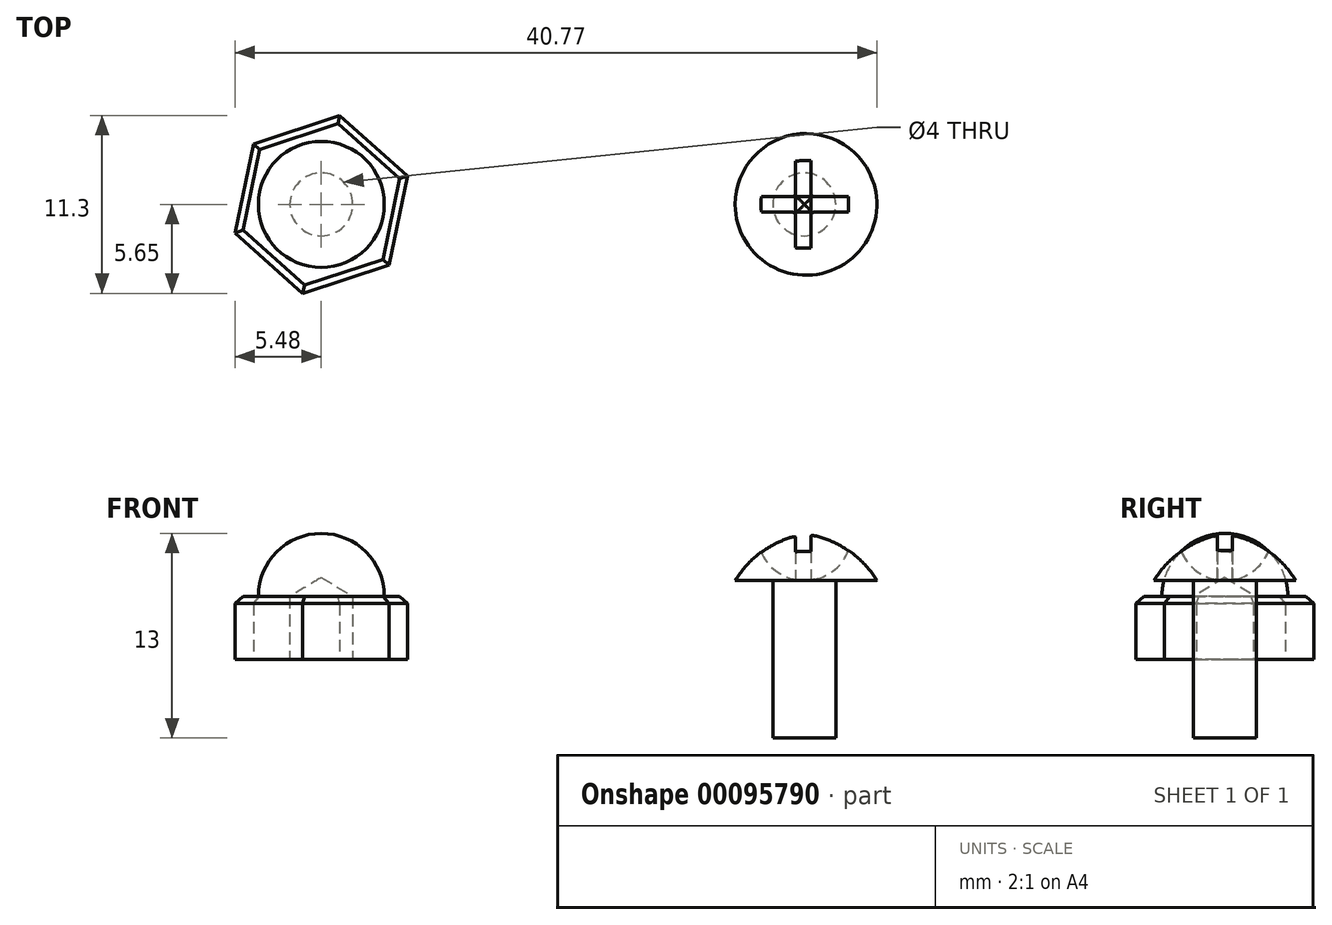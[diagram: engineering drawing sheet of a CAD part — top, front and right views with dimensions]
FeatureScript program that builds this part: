
annotation { "Feature Type Name" : "Feature", "Feature Type Description" : "" }
export const myFeature = defineFeature(function(context is Context, id is Id, definition is map)
    precondition{}
    {
        {
            var Q0;
            Q0=qCreatedBy(makeId("Top.planeOp"),FACE);
            var sketch = newSketch(context, id + "F0", { "sketchPlane" : qUnion([Q0])});
            skCircle(sketch, "E0.cCircle", {"center": v(0, 0) * mm, "radius": 5 * mm, "construction": true});
            skLineSegment(sketch, "E0.0", {"start": v(-4.3, 3.84) * mm, "end": v(1.17, 5.65) * mm});
            skLineSegment(sketch, "E0.1", {"start": v(1.17, 5.65) * mm, "end": v(5.48, 1.8) * mm});
            skLineSegment(sketch, "E0.2", {"start": v(5.48, 1.8) * mm, "end": v(4.3, -3.84) * mm});
            skLineSegment(sketch, "E0.3", {"start": v(4.3, -3.84) * mm, "end": v(-1.17, -5.65) * mm});
            skLineSegment(sketch, "E0.4", {"start": v(-1.17, -5.65) * mm, "end": v(-5.48, -1.8) * mm});
            skLineSegment(sketch, "E0.5", {"start": v(-5.48, -1.8) * mm, "end": v(-4.3, 3.84) * mm});
            skPoint(sketch, "E0.0.midPoint", {"position": v(-1.57, 4.75) * mm});
            skSolve(sketch);
        }
        {
            var Q0;
            Q0 = qSketchRegion(id + "F0", true);
            extrude(context, id + "F1", {"entities" : qUnion([Q0]), "depth" : 4 * mm});
        }
        {
            var Q0;
            Q0=makeQuery(id+"F1.opExtrude","CAP_FACE",FACE,{"disambiguationData":[OSD([sQuery(id+"F0.wireOp",EDGE,"E0.0"),sQuery(id+"F0.wireOp",EDGE,"E0.1"),sQuery(id+"F0.wireOp",EDGE,"E0.2"),sQuery(id+"F0.wireOp",EDGE,"E0.3"),sQuery(id+"F0.wireOp",EDGE,"E0.4"),sQuery(id+"F0.wireOp",EDGE,"E0.5")])],"isStart":false});
            var sketch = newSketch(context, id + "F2", { "sketchPlane" : qUnion([Q0])});
            skArc(sketch, "E1", {"start": v(-4, 0) * mm, "mid": v(0, 4) * mm, "end": v(4, 0) * mm});
            skLineSegment(sketch, "E2", {"start": v(-4, 0) * mm, "end": v(4, 0) * mm});
            skSolve(sketch);
        }
        {
            var Q0;
            Q0 = qSketchRegion(id + "F2", true);
            var Q1;
            Q1=sQuery(id+"F2.wireOp",EDGE,"E2");
            revolve(context, id + "F3", {"operationType" : NewBodyOperationType.ADD, "entities" : qUnion([Q0]), "axis" : qUnion([Q1]), "revolveType" : RevolveType.ONE_DIRECTION, "angle" : 180 * degree});
        }
        {
            var Q0;
            Q0=makeQuery(id+"F1.opExtrude","CAP_EDGE",EDGE,{"disambiguationData":[OSD([sQuery(id+"F0.wireOp",EDGE,"E0.5")])],"isStart":false});
            var Q1;
            Q1=makeQuery(id+"F1.opExtrude","CAP_EDGE",EDGE,{"disambiguationData":[OSD([sQuery(id+"F0.wireOp",EDGE,"E0.4")])],"isStart":false});
            var Q2;
            Q2=makeQuery(id+"F1.opExtrude","CAP_EDGE",EDGE,{"disambiguationData":[OSD([sQuery(id+"F0.wireOp",EDGE,"E0.3")])],"isStart":false});
            var Q3;
            Q3=makeQuery(id+"F1.opExtrude","CAP_EDGE",EDGE,{"disambiguationData":[OSD([sQuery(id+"F0.wireOp",EDGE,"E0.2")])],"isStart":false});
            var Q4;
            Q4=makeQuery(id+"F1.opExtrude","CAP_EDGE",EDGE,{"disambiguationData":[OSD([sQuery(id+"F0.wireOp",EDGE,"E0.1")])],"isStart":false});
            var Q5;
            Q5=makeQuery(id+"F1.opExtrude","CAP_EDGE",EDGE,{"disambiguationData":[OSD([sQuery(id+"F0.wireOp",EDGE,"E0.0")])],"isStart":false});
            chamfer(context, id + "F4", {"entities" : qUnion([Q0, Q1, Q2, Q3, Q4, Q5]), "width" : 0.46 * mm, "tangentPropagation" : true});
        }
        {
            var Q0;
            Q0=makeQuery(id+"F1.opExtrude","CAP_FACE",FACE,{"disambiguationData":[OSD([sQuery(id+"F0.wireOp",EDGE,"E0.0"),sQuery(id+"F0.wireOp",EDGE,"E0.1"),sQuery(id+"F0.wireOp",EDGE,"E0.2"),sQuery(id+"F0.wireOp",EDGE,"E0.3"),sQuery(id+"F0.wireOp",EDGE,"E0.4"),sQuery(id+"F0.wireOp",EDGE,"E0.5")])],"isStart":true});
            var sketch = newSketch(context, id + "F5", { "sketchPlane" : qUnion([Q0])});
            skPoint(sketch, "E3", {"position": v(0, 0) * mm});
            skSolve(sketch);
        }
        {
            var Q0;
            Q0=sQuery(id+"F5.wireOp",VERTEX,"E3");
            var Q1;
            Q1=makeQuery(id+"F1.opExtrude","SWEPT_BODY",BODY,{"disambiguationData":[OSD([sQuery(id+"F0.wireOp",EDGE,"E0.0"),sQuery(id+"F0.wireOp",EDGE,"E0.1"),sQuery(id+"F0.wireOp",EDGE,"E0.2"),sQuery(id+"F0.wireOp",EDGE,"E0.3"),sQuery(id+"F0.wireOp",EDGE,"E0.4"),sQuery(id+"F0.wireOp",EDGE,"E0.5")])]});
            hole(context, id + "F6", {"style" : HoleStyle.SIMPLE, "endStyle" : HoleEndStyle.BLIND, "holeDiameter" : 4 * mm, "holeDepth" : 4 * mm, "locations" : qUnion([Q0]), "scope" : qUnion([Q1])});
        }
        {
            var Q0;
            Q0=qCreatedBy(makeId("Top.planeOp"),FACE);
            var sketch = newSketch(context, id + "F7", { "sketchPlane" : qUnion([Q0])});
            skCircle(sketch, "E4", {"center": v(30.67, 0) * mm, "radius": 2 * mm});
            skSolve(sketch);
        }
        {
            var Q0;
            Q0 = qSketchRegion(id + "F7", true);
            extrude(context, id + "F8", {"entities" : qUnion([Q0]), "endBound" : BoundingType.SYMMETRIC, "depth" : 10 * mm});
        }
        {
            var Q0;
            Q0=qCreatedBy(makeId("Front.planeOp"),FACE);
            var sketch = newSketch(context, id + "F9", { "sketchPlane" : qUnion([Q0])});
            skLineSegment(sketch, "E5", {"start": v(30.79, 5) * mm, "end": v(26.29, 5) * mm});
            skLineSegment(sketch, "E6", {"start": v(30.79, 5) * mm, "end": v(30.79, 8) * mm});
            skArc(sketch, "E7", {"start": v(30.79, 8) * mm, "mid": v(28.2, 7) * mm, "end": v(26.29, 5) * mm});
            skSolve(sketch);
        }
        {
            var Q0;
            Q0 = qSketchRegion(id + "F9", true);
            var Q1;
            Q1=sQuery(id+"F9.wireOp",EDGE,"E6");
            revolve(context, id + "F10", {"entities" : qUnion([Q0]), "axis" : qUnion([Q1]), "revolveType" : RevolveType.FULL});
        }
        {
            var Q0;
            Q0=makeQuery(id+"F10.opRevolve","SWEPT_FACE",FACE,{"disambiguationData":[OSD([sQuery(id+"F9.wireOp",EDGE,"E5")])]});
            var sketch = newSketch(context, id + "F11", { "sketchPlane" : qUnion([Q0])});
            skPoint(sketch, "E8", {"position": v(30.67, 0) * mm});
            skSolve(sketch);
        }
        {
            var Q0;
            Q0=qCreatedBy(makeId("Top.planeOp"),FACE);
            var Q1;
            Q1=makeQuery(id+"F10.opRevolve","SWEPT_VERTEX",VERTEX,{"disambiguationData":[OSD([sQuery(id+"F9.wireOp",EDGE,"E6"),sQuery(id+"F9.wireOp",EDGE,"E7")])]});
            var Q2;
            Q2 = qBodyType(qCreatedBy(id + "F11" ,EDGE), BodyType.WIRE);
            cPlane(context, id + "F12", {"entities" : qUnion([Q0, Q1, Q2]), "cplaneType" : CPlaneType.PLANE_POINT, "offset" : 152.4 * mm, "width" : 152.4 * mm, "height" : 152.4 * mm});
        }
        {
            var Q0;
            Q0=qCreatedBy(id+"F12.planeOp",FACE);
            var sketch = newSketch(context, id + "F13", { "sketchPlane" : qUnion([Q0])});
            skPoint(sketch, "E9.middle", {"position": v(30.69, 0) * mm});
            skLineSegment(sketch, "E10.bottom", {"start": v(30.69, 0.48) * mm, "end": v(27.69, 0.48) * mm});
            skLineSegment(sketch, "E10.top", {"start": v(30.69, -0.48) * mm, "end": v(27.69, -0.48) * mm});
            skLineSegment(sketch, "E10.left", {"start": v(30.69, 0.48) * mm, "end": v(30.69, -0.48) * mm});
            skLineSegment(sketch, "E10.right", {"start": v(27.69, 0.48) * mm, "end": v(27.69, -0.48) * mm});
            skPoint(sketch, "E10.middle", {"position": v(29.19, 0) * mm});
            skSolve(sketch);
        }
        {
            var Q0;
            Q0 = qSketchRegion(id + "F13", true);
            var Q1;
            Q1=sQuery(id+"F13.wireOp",EDGE,"E10.left");
            revolve(context, id + "F14", {"operationType" : NewBodyOperationType.REMOVE, "entities" : qUnion([Q0]), "axis" : qUnion([Q1]), "revolveType" : RevolveType.FULL, "oppositeDirection" : true});
        }
        {
            var Q0;
            Q0=qCreatedBy(id+"F12.planeOp",FACE);
            var sketch = newSketch(context, id + "F15", { "sketchPlane" : qUnion([Q0])});
            skLineSegment(sketch, "E11.bottom", {"start": v(31.09, 0) * mm, "end": v(30.12, 0) * mm});
            skLineSegment(sketch, "E11.top", {"start": v(31.09, 3) * mm, "end": v(30.12, 3) * mm});
            skLineSegment(sketch, "E11.left", {"start": v(31.09, 0) * mm, "end": v(31.09, 3) * mm});
            skLineSegment(sketch, "E11.right", {"start": v(30.12, 0) * mm, "end": v(30.12, 3) * mm});
            skPoint(sketch, "E11.middle", {"position": v(30.6, 1.5) * mm});
            skSolve(sketch);
        }
        {
            var Q0;
            Q0 = qSketchRegion(id + "F15", true);
            var Q1;
            Q1=sQuery(id+"F15.wireOp",EDGE,"E11.bottom");
            revolve(context, id + "F16", {"operationType" : NewBodyOperationType.REMOVE, "entities" : qUnion([Q0]), "axis" : qUnion([Q1]), "revolveType" : RevolveType.FULL, "oppositeDirection" : true});
        }
        {
            var Q0;
            Q0=makeQuery(id+"F16.boolean.opBoolean","INTERSECT",EDGE,{"derivedFrom":[makeQuery(id+"F14.boolean.opBoolean","COPY",FACE,{"derivedFrom":makeQuery(id+"F14.opRevolve","SWEPT_FACE",FACE,{"disambiguationData":[OSD([sQuery(id+"F13.wireOp",EDGE,"E10.bottom")])]})}),makeQuery(id+"F16.opRevolve","SWEPT_FACE",FACE,{"disambiguationData":[OSD([sQuery(id+"F15.wireOp",EDGE,"E11.right")])]})]});
            var Q1;
            Q1=makeQuery(id+"F16.boolean.opBoolean","INTERSECT",EDGE,{"derivedFrom":[makeQuery(id+"F14.boolean.opBoolean","COPY",FACE,{"derivedFrom":makeQuery(id+"F14.opRevolve","SWEPT_FACE",FACE,{"disambiguationData":[OSD([sQuery(id+"F13.wireOp",EDGE,"E10.bottom")])]})}),makeQuery(id+"F16.opRevolve","SWEPT_FACE",FACE,{"disambiguationData":[OSD([sQuery(id+"F15.wireOp",EDGE,"E11.left")])]})]});
            var Q2;
            Q2=makeQuery(id+"F16.boolean.opBoolean","INTERSECT",EDGE,{"derivedFrom":[makeQuery(id+"F14.boolean.opBoolean","COPY",FACE,{"derivedFrom":makeQuery(id+"F14.opRevolve","SWEPT_FACE",FACE,{"disambiguationData":[OSD([sQuery(id+"F13.wireOp",EDGE,"E10.top")])]})}),makeQuery(id+"F16.opRevolve","SWEPT_FACE",FACE,{"disambiguationData":[OSD([sQuery(id+"F15.wireOp",EDGE,"E11.left")])]})]});
            var Q3;
            Q3=makeQuery(id+"F16.boolean.opBoolean","INTERSECT",EDGE,{"derivedFrom":[makeQuery(id+"F14.boolean.opBoolean","COPY",FACE,{"derivedFrom":makeQuery(id+"F14.opRevolve","SWEPT_FACE",FACE,{"disambiguationData":[OSD([sQuery(id+"F13.wireOp",EDGE,"E10.top")])]})}),makeQuery(id+"F16.opRevolve","SWEPT_FACE",FACE,{"disambiguationData":[OSD([sQuery(id+"F15.wireOp",EDGE,"E11.right")])]})]});
            fillet(context, id + "F17", {"entities" : qUnion([Q0, Q1, Q2, Q3]), "radius" : 0.25 * mm, "tangentPropagation" : true, "allowEdgeOverflow" : false});
        }
    });
